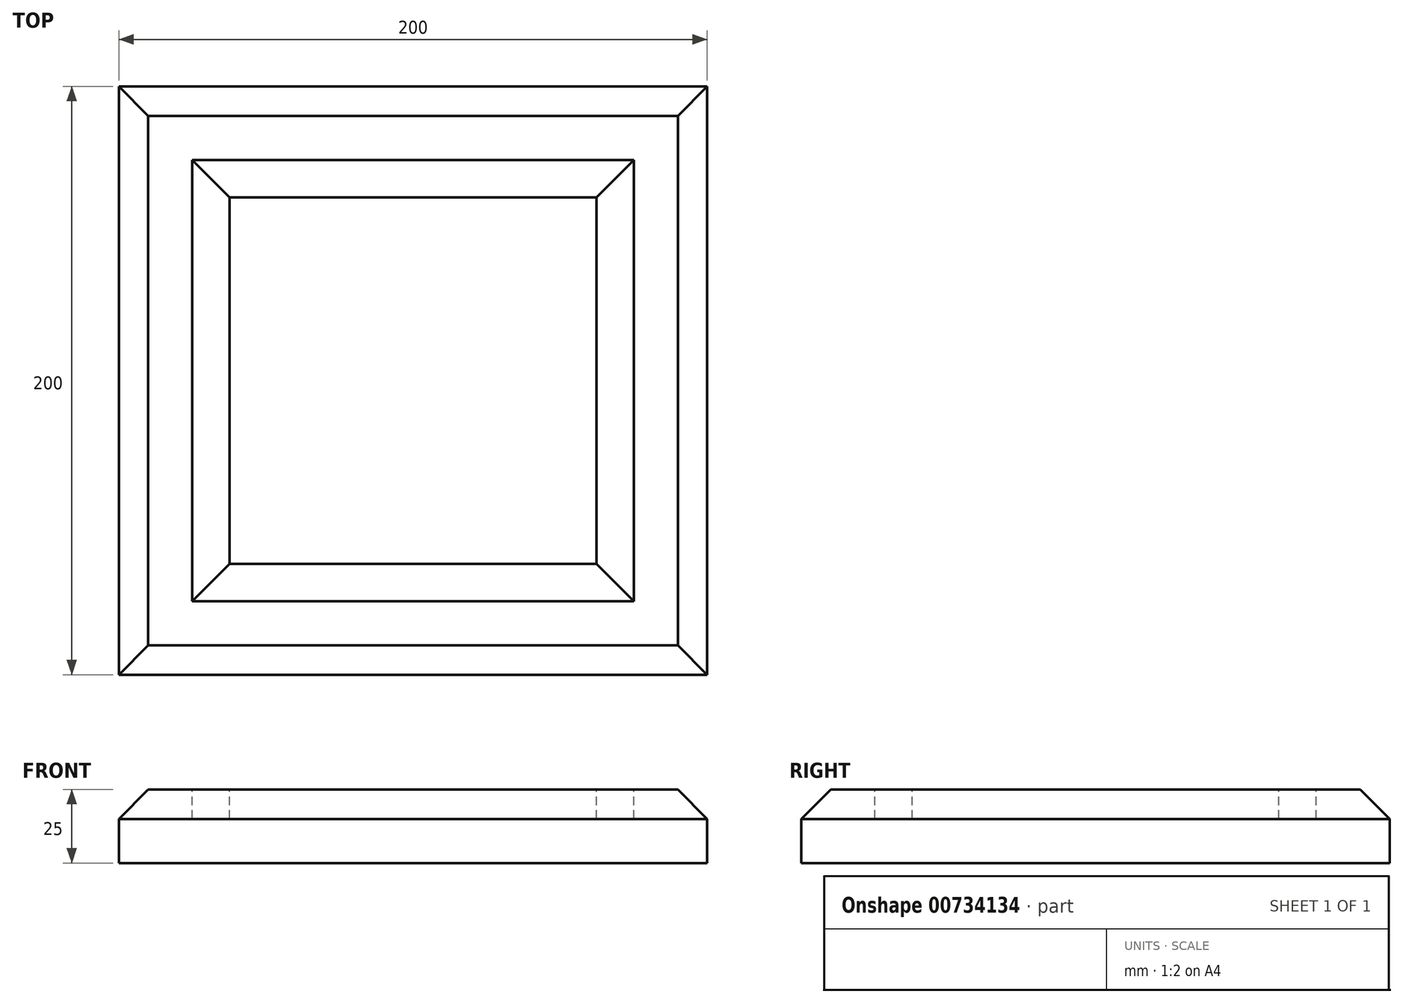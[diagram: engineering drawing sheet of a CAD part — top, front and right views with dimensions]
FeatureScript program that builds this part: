
annotation { "Feature Type Name" : "Feature", "Feature Type Description" : "" }
export const myFeature = defineFeature(function(context is Context, id is Id, definition is map)
    precondition{}
    {
        {
            var Q0;
            Q0=qCreatedBy(makeId("Top.planeOp"),FACE);
            var sketch = newSketch(context, id + "F0", { "sketchPlane" : qUnion([Q0])});
            skLineSegment(sketch, "E0.bottom", {"start": v(-100, 100) * mm, "end": v(100, 100) * mm});
            skLineSegment(sketch, "E0.top", {"start": v(-100, -100) * mm, "end": v(100, -100) * mm});
            skLineSegment(sketch, "E0.left", {"start": v(-100, 100) * mm, "end": v(-100, -100) * mm});
            skLineSegment(sketch, "E0.right", {"start": v(100, 100) * mm, "end": v(100, -100) * mm});
            skPoint(sketch, "E0.middle", {"position": v(0, 0) * mm});
            skSolve(sketch);
        }
        {
            var Q0;
            Q0 = qSketchRegion(id + "F0", true);
            extrude(context, id + "F1", {"entities" : qUnion([Q0]), "oppositeDirection" : true, "depth" : 25 * mm, "offsetDistance" : 25 * mm});
        }
        {
            var Q0;
            Q0=makeQuery(id+"F1.opExtrude","CAP_EDGE",EDGE,{"disambiguationData":[OSD([sQuery(id+"F0.wireOp",EDGE,"E0.left")])],"isStart":true});
            var Q1;
            Q1=makeQuery(id+"F1.opExtrude","CAP_EDGE",EDGE,{"disambiguationData":[OSD([sQuery(id+"F0.wireOp",EDGE,"E0.bottom")])],"isStart":true});
            var Q2;
            Q2=makeQuery(id+"F1.opExtrude","CAP_EDGE",EDGE,{"disambiguationData":[OSD([sQuery(id+"F0.wireOp",EDGE,"E0.top")])],"isStart":true});
            var Q3;
            Q3=makeQuery(id+"F1.opExtrude","CAP_EDGE",EDGE,{"disambiguationData":[OSD([sQuery(id+"F0.wireOp",EDGE,"E0.right")])],"isStart":true});
            chamfer(context, id + "F2", {"entities" : qUnion([Q0, Q1, Q2, Q3]), "width" : 10 * mm, "tangentPropagation" : true});
        }
        {
            var Q0;
            Q0=makeQuery(id+"F1.opExtrude","CAP_FACE",FACE,{"disambiguationData":[OSD([sQuery(id+"F0.wireOp",EDGE,"E0.bottom"),sQuery(id+"F0.wireOp",EDGE,"E0.top"),sQuery(id+"F0.wireOp",EDGE,"E0.left"),sQuery(id+"F0.wireOp",EDGE,"E0.right")])],"isStart":true});
            var sketch = newSketch(context, id + "F3", { "sketchPlane" : qUnion([Q0])});
            skLineSegment(sketch, "E1.bottom", {"start": v(-62.3, 62.3) * mm, "end": v(62.3, 62.3) * mm});
            skLineSegment(sketch, "E1.top", {"start": v(-62.3, -62.3) * mm, "end": v(62.3, -62.3) * mm});
            skLineSegment(sketch, "E1.left", {"start": v(-62.3, 62.3) * mm, "end": v(-62.3, -62.3) * mm});
            skLineSegment(sketch, "E1.right", {"start": v(62.3, 62.3) * mm, "end": v(62.3, -62.3) * mm});
            skPoint(sketch, "E1.middle", {"position": v(0, 0) * mm});
            skLineSegment(sketch, "E2.bottom", {"start": v(-75, 75) * mm, "end": v(75, 75) * mm});
            skLineSegment(sketch, "E2.top", {"start": v(-75, -75) * mm, "end": v(75, -75) * mm});
            skLineSegment(sketch, "E2.left", {"start": v(-75, 75) * mm, "end": v(-75, -75) * mm});
            skLineSegment(sketch, "E2.right", {"start": v(75, 75) * mm, "end": v(75, -75) * mm});
            skLineSegment(sketch, "E3", {"start": v(-62.3, 62.3) * mm, "end": v(-62.3, 75) * mm, "construction": true});
            skLineSegment(sketch, "E4", {"start": v(-62.3, 62.3) * mm, "end": v(-75, 62.3) * mm, "construction": true});
            skPoint(sketch, "E5", {"position": v(0, 100) * mm});
            skPoint(sketch, "E6", {"position": v(-100, 0) * mm});
            skSolve(sketch);
        }
        {
            var Q0;
            Q0 = qSketchRegion(id + "F3", true);
            extrude(context, id + "F4", {"entities" : qUnion([Q0]), "operationType" : NewBodyOperationType.REMOVE, "oppositeDirection" : true, "depth" : 10 * mm, "offsetDistance" : 25 * mm});
        }
        {
            var Q0;
            Q0=makeQuery(id+"F4.boolean.opBoolean","SPLIT",FACE,{"disambiguationData":[TD([makeQuery(id+"F4.opExtrude","SWEPT_FACE",FACE,{"disambiguationData":[OSD([sQuery(id+"F3.wireOp",EDGE,"E1.bottom")])]})])],"derivedFrom":makeQuery(id+"F1.opExtrude","CAP_FACE",FACE,{"disambiguationData":[OSD([sQuery(id+"F0.wireOp",EDGE,"E0.bottom"),sQuery(id+"F0.wireOp",EDGE,"E0.top"),sQuery(id+"F0.wireOp",EDGE,"E0.left"),sQuery(id+"F0.wireOp",EDGE,"E0.right")])],"isStart":true})});
            var sketch = newSketch(context, id + "F5", { "sketchPlane" : qUnion([Q0])});
            skLineSegment(sketch, "E7", {"start": v(-62.3, -62.3) * mm, "end": v(-75, -75) * mm});
            skLineSegment(sketch, "E8", {"start": v(-75, -75) * mm, "end": v(-75, 75) * mm});
            skLineSegment(sketch, "E9", {"start": v(-75, 75) * mm, "end": v(-62.3, 62.3) * mm});
            skLineSegment(sketch, "E10", {"start": v(-62.3, 62.3) * mm, "end": v(-62.3, -62.3) * mm});
            skLineSegment(sketch, "E11", {"start": v(-75, 75) * mm, "end": v(75, 75) * mm});
            skLineSegment(sketch, "E12", {"start": v(75, 75) * mm, "end": v(62.3, 62.3) * mm});
            skLineSegment(sketch, "E13", {"start": v(62.3, 62.3) * mm, "end": v(-62.3, 62.3) * mm});
            skLineSegment(sketch, "E14", {"start": v(75, 75) * mm, "end": v(75, -75) * mm});
            skLineSegment(sketch, "E15", {"start": v(75, -75) * mm, "end": v(62.3, -62.3) * mm});
            skLineSegment(sketch, "E16", {"start": v(62.3, -62.3) * mm, "end": v(62.3, 62.3) * mm});
            skLineSegment(sketch, "E17", {"start": v(62.3, -62.3) * mm, "end": v(-62.3, -62.3) * mm});
            skLineSegment(sketch, "E18", {"start": v(-75, -75) * mm, "end": v(75, -75) * mm});
            skSolve(sketch);
        }
        {
            var Q0;
            Q0=makeQuery(id+"F5.imprint","IMPRINT",FACE,{"disambiguationData":[TD([[makeQuery(id+"F5.imprint","IMPRINT",EDGE,{"derivedFrom":sQuery(id+"F5.wireOp",EDGE,"E7")}),-1.0]])]});
            var Q1;
            Q1=makeQuery(id+"F4.boolean.opBoolean","COPY",FACE,{"derivedFrom":makeQuery(id+"F4.opExtrude","CAP_FACE",FACE,{"disambiguationData":[OSD([sQuery(id+"F3.wireOp",EDGE,"E1.bottom"),sQuery(id+"F3.wireOp",EDGE,"E1.top"),sQuery(id+"F3.wireOp",EDGE,"E1.left"),sQuery(id+"F3.wireOp",EDGE,"E1.right"),sQuery(id+"F3.wireOp",EDGE,"E2.bottom"),sQuery(id+"F3.wireOp",EDGE,"E2.top"),sQuery(id+"F3.wireOp",EDGE,"E2.left"),sQuery(id+"F3.wireOp",EDGE,"E2.right")])],"isStart":false})});
            extrude(context, id + "F6", {"entities" : qUnion([Q0]), "endBound" : BoundingType.UP_TO_SURFACE, "oppositeDirection" : true, "depth" : 25 * mm, "endBoundEntityFace" : qUnion([Q1]), "offsetDistance" : 25 * mm});
        }
        {
            var Q0;
            Q0=makeQuery(id+"F5.imprint","IMPRINT",FACE,{"disambiguationData":[TD([[makeQuery(id+"F5.imprint","IMPRINT",EDGE,{"derivedFrom":sQuery(id+"F5.wireOp",EDGE,"E7")}),1.0]])]});
            var Q1;
            Q1=makeQuery(id+"F4.boolean.opBoolean","COPY",FACE,{"derivedFrom":makeQuery(id+"F4.opExtrude","CAP_FACE",FACE,{"disambiguationData":[OSD([sQuery(id+"F3.wireOp",EDGE,"E1.bottom"),sQuery(id+"F3.wireOp",EDGE,"E1.top"),sQuery(id+"F3.wireOp",EDGE,"E1.left"),sQuery(id+"F3.wireOp",EDGE,"E1.right"),sQuery(id+"F3.wireOp",EDGE,"E2.bottom"),sQuery(id+"F3.wireOp",EDGE,"E2.top"),sQuery(id+"F3.wireOp",EDGE,"E2.left"),sQuery(id+"F3.wireOp",EDGE,"E2.right")])],"isStart":false})});
            extrude(context, id + "F7", {"entities" : qUnion([Q0]), "endBound" : BoundingType.UP_TO_SURFACE, "oppositeDirection" : true, "depth" : 25 * mm, "endBoundEntityFace" : qUnion([Q1]), "offsetDistance" : 25 * mm});
        }
        {
            var Q0;
            Q0=makeQuery(id+"F5.imprint","IMPRINT",FACE,{"disambiguationData":[TD([[makeQuery(id+"F5.imprint","IMPRINT",EDGE,{"derivedFrom":sQuery(id+"F5.wireOp",EDGE,"E12")}),1.0]])]});
            var Q1;
            Q1=makeQuery(id+"F4.boolean.opBoolean","COPY",FACE,{"derivedFrom":makeQuery(id+"F4.opExtrude","CAP_FACE",FACE,{"disambiguationData":[OSD([sQuery(id+"F3.wireOp",EDGE,"E1.bottom"),sQuery(id+"F3.wireOp",EDGE,"E1.top"),sQuery(id+"F3.wireOp",EDGE,"E1.left"),sQuery(id+"F3.wireOp",EDGE,"E1.right"),sQuery(id+"F3.wireOp",EDGE,"E2.bottom"),sQuery(id+"F3.wireOp",EDGE,"E2.top"),sQuery(id+"F3.wireOp",EDGE,"E2.left"),sQuery(id+"F3.wireOp",EDGE,"E2.right")])],"isStart":false})});
            extrude(context, id + "F8", {"entities" : qUnion([Q0]), "endBound" : BoundingType.UP_TO_SURFACE, "oppositeDirection" : true, "depth" : 25 * mm, "endBoundEntityFace" : qUnion([Q1]), "offsetDistance" : 25 * mm});
        }
        {
            var Q0;
            Q0=makeQuery(id+"F5.imprint","IMPRINT",FACE,{"disambiguationData":[TD([[makeQuery(id+"F5.imprint","IMPRINT",EDGE,{"derivedFrom":sQuery(id+"F5.wireOp",EDGE,"E9")}),1.0]])]});
            var Q1;
            Q1=makeQuery(id+"F4.boolean.opBoolean","COPY",FACE,{"derivedFrom":makeQuery(id+"F4.opExtrude","CAP_FACE",FACE,{"disambiguationData":[OSD([sQuery(id+"F3.wireOp",EDGE,"E1.bottom"),sQuery(id+"F3.wireOp",EDGE,"E1.top"),sQuery(id+"F3.wireOp",EDGE,"E1.left"),sQuery(id+"F3.wireOp",EDGE,"E1.right"),sQuery(id+"F3.wireOp",EDGE,"E2.bottom"),sQuery(id+"F3.wireOp",EDGE,"E2.top"),sQuery(id+"F3.wireOp",EDGE,"E2.left"),sQuery(id+"F3.wireOp",EDGE,"E2.right")])],"isStart":false})});
            extrude(context, id + "F9", {"entities" : qUnion([Q0]), "endBound" : BoundingType.UP_TO_SURFACE, "oppositeDirection" : true, "depth" : 25 * mm, "endBoundEntityFace" : qUnion([Q1]), "offsetDistance" : 25 * mm});
        }
    });
